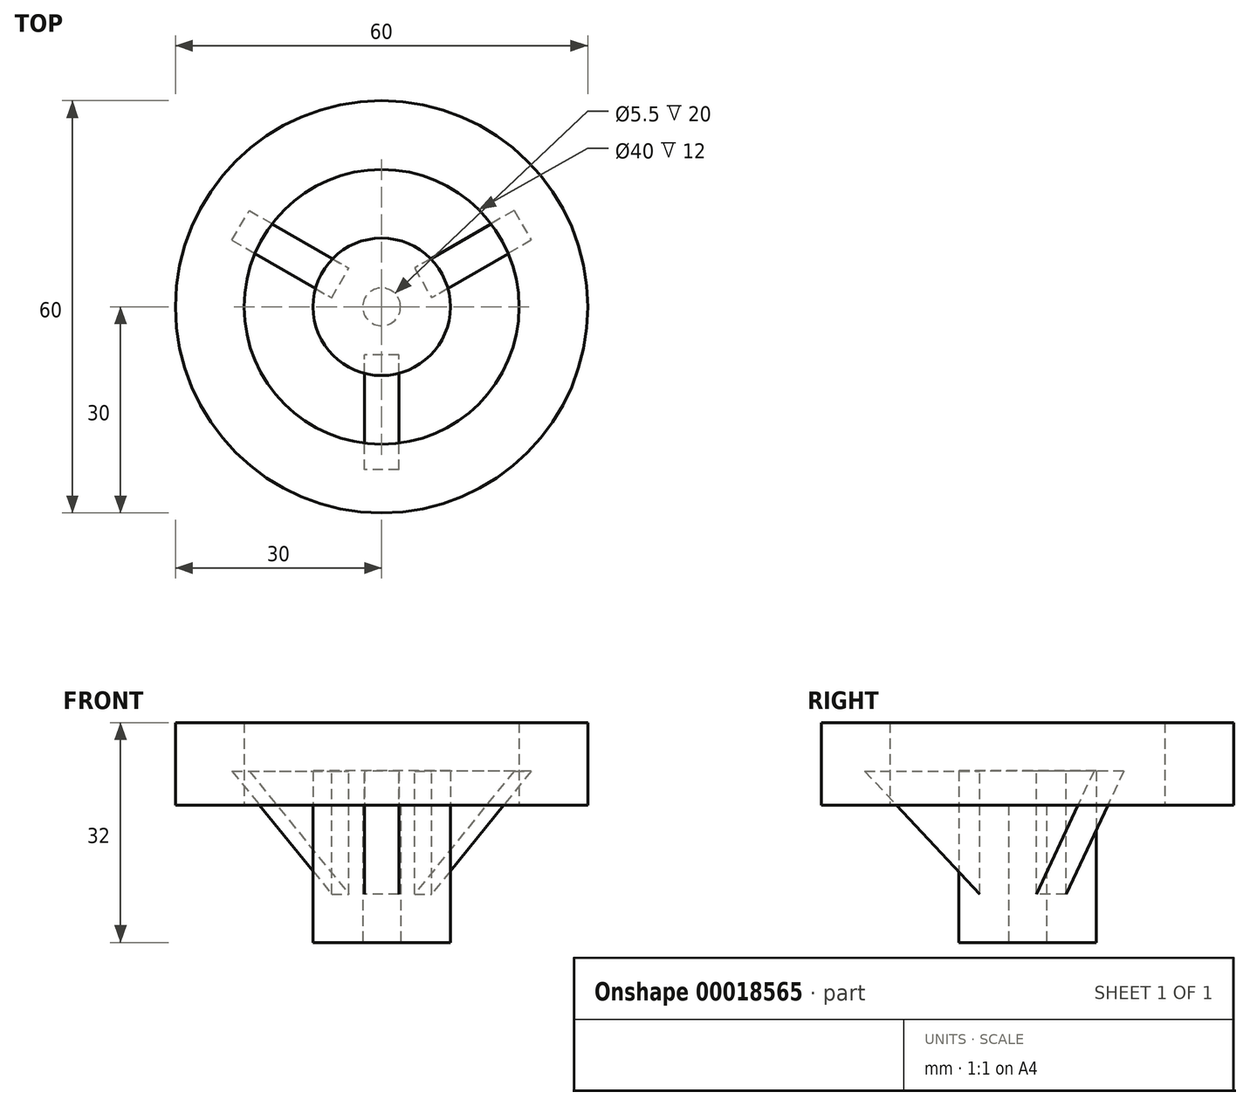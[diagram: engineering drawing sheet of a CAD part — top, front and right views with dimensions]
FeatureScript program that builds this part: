
annotation { "Feature Type Name" : "Feature", "Feature Type Description" : "" }
export const myFeature = defineFeature(function(context is Context, id is Id, definition is map)
    precondition{}
    {
        {
            var Q0;
            Q0=qCreatedBy(makeId("Top.planeOp"),FACE);
            var sketch = newSketch(context, id + "F0", { "sketchPlane" : qUnion([Q0])});
            skCircle(sketch, "E0", {"center": v(0, 0) * mm, "radius": 30 * mm});
            skCircle(sketch, "E1", {"center": v(0, 0) * mm, "radius": 20 * mm});
            skSolve(sketch);
        }
        {
            var Q0;
            Q0 = qSketchRegion(id + "F0", true);
            extrude(context, id + "F1", {"entities" : qUnion([Q0]), "depth" : 12 * mm});
        }
        {
            var Q0;
            Q0=qCreatedBy(makeId("Top.planeOp"),FACE);
            var sketch = newSketch(context, id + "F2", { "sketchPlane" : qUnion([Q0])});
            skCircle(sketch, "E2", {"center": v(0, 0) * mm, "radius": 10 * mm});
            skSolve(sketch);
        }
        {
            var Q0;
            Q0 = qSketchRegion(id + "F2", true);
            extrude(context, id + "F3", {"entities" : qUnion([Q0]), "depth" : 5 * mm, "hasSecondDirection" : true, "secondDirectionOppositeDirection" : true, "secondDirectionDepth" : 20 * mm});
        }
        {
            var Q0;
            Q0=qCreatedBy(makeId("Right.planeOp"),FACE);
            var sketch = newSketch(context, id + "F4", { "sketchPlane" : qUnion([Q0])});
            skLineSegment(sketch, "E3", {"start": v(-23.7, 4.95) * mm, "end": v(-6.96, -12.96) * mm});
            skLineSegment(sketch, "E4", {"start": v(-6.96, -12.96) * mm, "end": v(-6.96, 4.95) * mm});
            skLineSegment(sketch, "E5", {"start": v(-23.7, 4.95) * mm, "end": v(-6.96, 4.95) * mm});
            skSolve(sketch);
        }
        {
            var Q0;
            Q0 = qSketchRegion(id + "F4", true);
            extrude(context, id + "F5", {"entities" : qUnion([Q0]), "endBound" : BoundingType.SYMMETRIC, "depth" : 5 * mm});
        }
        {
            var Q0;
            Q0=makeQuery(id+"F5.opExtrude","SWEPT_BODY",BODY,{"disambiguationData":[OSD([sQuery(id+"F4.wireOp",EDGE,"E3"),sQuery(id+"F4.wireOp",EDGE,"E4"),sQuery(id+"F4.wireOp",EDGE,"E5")])]});
            var Q1;
            Q1=makeQuery(id+"F3.opExtrude","SWEPT_FACE",FACE,{"disambiguationData":[OSD([sQuery(id+"F2.wireOp",EDGE,"E2")])]});
            circularPattern(context, id + "F6", {"entities" : qUnion([Q0]), "axis" : qUnion([Q1]), "angle" : 120 * degree, "instanceCount" : 3});
        }
        {
            var Q0;
            Q0=makeQuery(id+"F3.opExtrude","CAP_FACE",FACE,{"disambiguationData":[OSD([sQuery(id+"F2.wireOp",EDGE,"E2")])],"isStart":true});
            var sketch = newSketch(context, id + "F7", { "sketchPlane" : qUnion([Q0])});
            skCircle(sketch, "E6", {"center": v(0, 0) * mm, "radius": 2.75 * mm});
            skSolve(sketch);
        }
        {
            var Q0;
            Q0=makeQuery(id+"F7.imprint","IMPRINT",FACE,{"disambiguationData":[TD([[makeQuery(id+"F7.imprint","IMPRINT",EDGE,{"derivedFrom":sQuery(id+"F7.wireOp",EDGE,"E6")}),1.0]])]});
            extrude(context, id + "F8", {"entities" : qUnion([Q0]), "operationType" : NewBodyOperationType.REMOVE, "oppositeDirection" : true, "depth" : 20 * mm});
        }
    });
